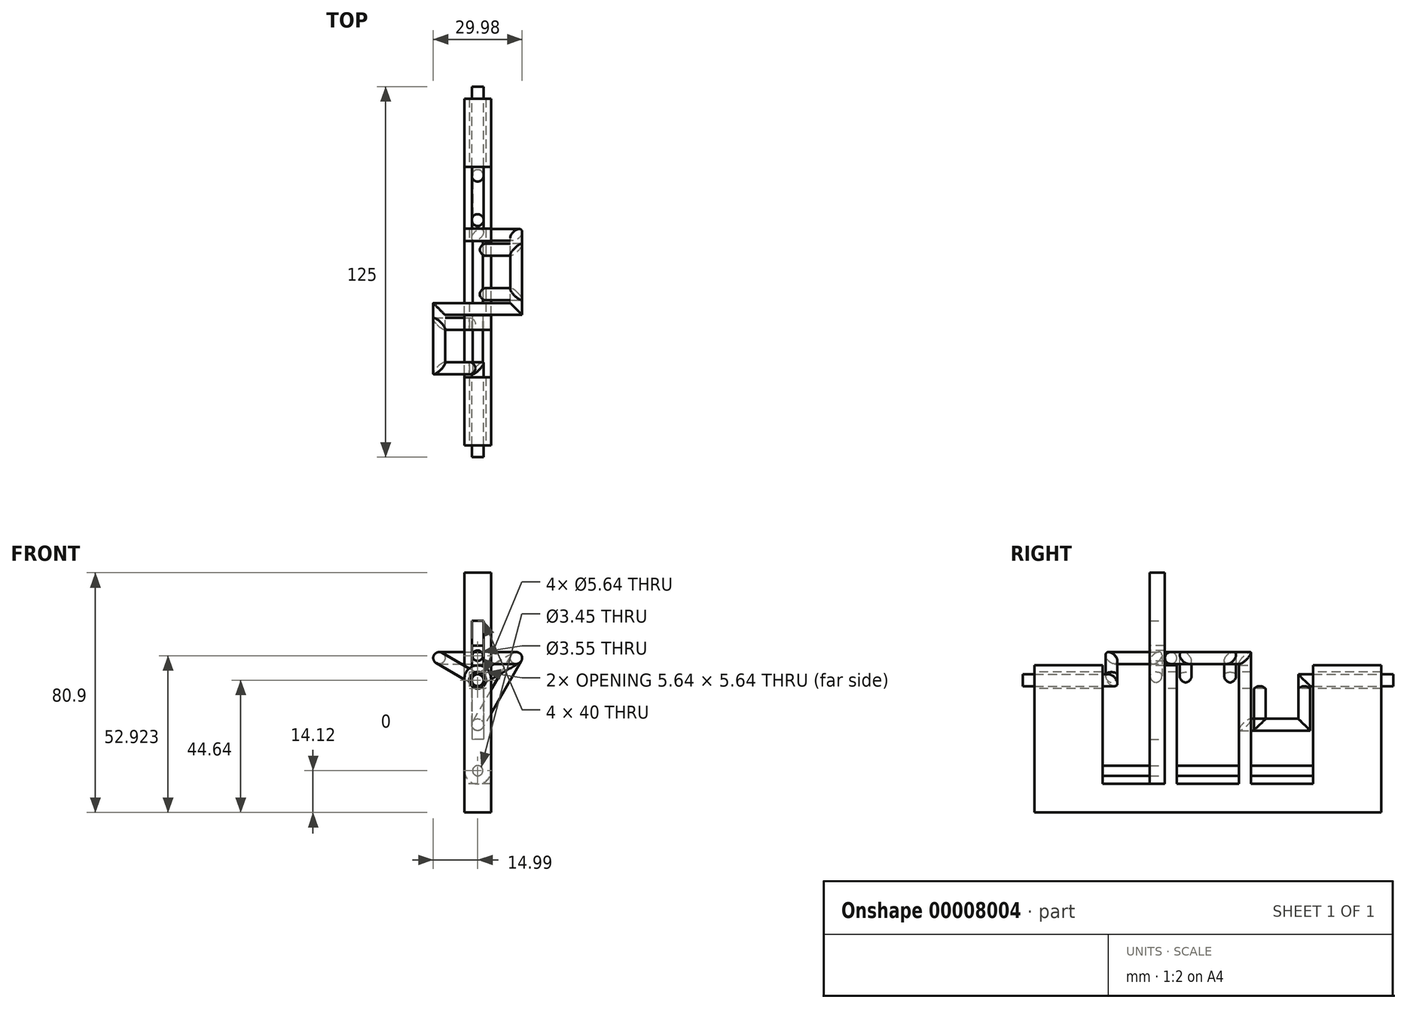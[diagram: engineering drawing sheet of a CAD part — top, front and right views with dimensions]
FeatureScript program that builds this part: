
annotation { "Feature Type Name" : "Feature", "Feature Type Description" : "" }
export const myFeature = defineFeature(function(context is Context, id is Id, definition is map)
    precondition{}
    {
        {
            var Q0;
            Q0=qCreatedBy(makeId("Front.planeOp"),FACE);
            var sketch = newSketch(context, id + "F0", { "sketchPlane" : qUnion([Q0])});
            skCircle(sketch, "E0", {"center": v(0, 0) * mm, "radius": 2 * mm});
            skLineSegment(sketch, "E1", {"start": v(0, 0) * mm, "end": v(-13, 7.5) * mm, "construction": true});
            skLineSegment(sketch, "E2", {"start": v(0, 0) * mm, "end": v(13, 7.5) * mm, "construction": true});
            skLineSegment(sketch, "E3", {"start": v(0, 0) * mm, "end": v(0, -15) * mm, "construction": true});
            skSolve(sketch);
        }
        {
            var Q0;
            Q0=qCreatedBy(makeId("Top.planeOp"),FACE);
            var sketch = newSketch(context, id + "F1", { "sketchPlane" : qUnion([Q0])});
            skLineSegment(sketch, "E4", {"start": v(0, 0) * mm, "end": v(0, 30) * mm});
            skLineSegment(sketch, "E5", {"start": v(0, 45) * mm, "end": v(0, 55) * mm});
            skLineSegment(sketch, "E6", {"start": v(0, 70) * mm, "end": v(0, 80) * mm});
            skLineSegment(sketch, "E7", {"start": v(0, 95) * mm, "end": v(0, 125) * mm});
            skLineSegment(sketch, "E8", {"start": v(0, 30) * mm, "end": v(0, 45) * mm, "construction": true});
            skLineSegment(sketch, "E9", {"start": v(0, 55) * mm, "end": v(0, 70) * mm, "construction": true});
            skLineSegment(sketch, "E10", {"start": v(0, 80) * mm, "end": v(0, 95) * mm, "construction": true});
            skSolve(sketch);
        }
        {
            var Q0;
            Q0=sQuery(id+"F0.wireOp",VERTEX,"E1.end");
            var Q1;
            Q1=sQuery(id+"F0.wireOp",VERTEX,"E2.start");
            var Q2;
            Q2=sQuery(id+"F1.wireOp",VERTEX,"E8.start");
            cPlane(context, id + "F2", {"entities" : qUnion([Q0, Q1, Q2]), "cplaneType" : CPlaneType.THREE_POINT, "offset" : 150 * mm, "width" : 150 * mm, "height" : 150 * mm});
        }
        {
            var Q0;
            Q0=sQuery(id+"F0.wireOp",VERTEX,"E2.end");
            var Q1;
            Q1=sQuery(id+"F0.wireOp",VERTEX,"E2.start");
            var Q2;
            Q2=sQuery(id+"F1.wireOp",VERTEX,"E8.start");
            cPlane(context, id + "F3", {"entities" : qUnion([Q0, Q1, Q2]), "cplaneType" : CPlaneType.THREE_POINT, "offset" : 150 * mm, "width" : 150 * mm, "height" : 150 * mm});
        }
        {
            var Q0;
            Q0=qCreatedBy(id+"F2.planeOp",FACE);
            var sketch = newSketch(context, id + "F4", { "sketchPlane" : qUnion([Q0])});
            skLineSegment(sketch, "E11.0", {"start": v(0, 0) * mm, "end": v(-15, 0) * mm, "construction": true});
            skLineSegment(sketch, "E12.0", {"start": v(0, -30) * mm, "end": v(0, -45) * mm, "construction": true});
            skLineSegment(sketch, "E13", {"start": v(0, -30) * mm, "end": v(-15, -30) * mm});
            skLineSegment(sketch, "E14", {"start": v(-15, -30) * mm, "end": v(-15, -45) * mm});
            skLineSegment(sketch, "E15", {"start": v(-15, -45) * mm, "end": v(0, -45) * mm});
            skSolve(sketch);
        }
        {
            var Q0;
            Q0=qCreatedBy(id+"F3.planeOp",FACE);
            var sketch = newSketch(context, id + "F5", { "sketchPlane" : qUnion([Q0])});
            skLineSegment(sketch, "E16.0", {"start": v(0, 0) * mm, "end": v(15, 0) * mm, "construction": true});
            skLineSegment(sketch, "E16.1", {"start": v(0, 55) * mm, "end": v(0, 70) * mm, "construction": true});
            skLineSegment(sketch, "E17", {"start": v(0, 55) * mm, "end": v(15, 55) * mm});
            skLineSegment(sketch, "E18", {"start": v(15, 55) * mm, "end": v(15, 70) * mm});
            skLineSegment(sketch, "E19", {"start": v(15, 70) * mm, "end": v(0, 70) * mm});
            skSolve(sketch);
        }
        {
            var Q0;
            Q0=qCreatedBy(makeId("Right.planeOp"),FACE);
            var sketch = newSketch(context, id + "F6", { "sketchPlane" : qUnion([Q0])});
            skLineSegment(sketch, "E20.0", {"start": v(0, 0) * mm, "end": v(0, -15) * mm, "construction": true});
            skLineSegment(sketch, "E20.1", {"start": v(80, 0) * mm, "end": v(95, 0) * mm, "construction": true});
            skLineSegment(sketch, "E21", {"start": v(80, 0) * mm, "end": v(80, -15) * mm});
            skLineSegment(sketch, "E22", {"start": v(80, -15) * mm, "end": v(95, -15) * mm});
            skLineSegment(sketch, "E23", {"start": v(95, -15) * mm, "end": v(95, 0) * mm});
            skSolve(sketch);
        }
        {
            var Q0;
            Q0=makeQuery(id+"F0.imprint","IMPRINT",FACE,{"disambiguationData":[TD([[makeQuery(id+"F0.imprint","IMPRINT",EDGE,{"derivedFrom":sQuery(id+"F0.wireOp",EDGE,"E0")}),1.0]])]});
            var Q1;
            Q1=sQuery(id+"F1.wireOp",EDGE,"E4");
            var Q2;
            Q2=sQuery(id+"F4.wireOp",EDGE,"E13");
            var Q3;
            Q3=sQuery(id+"F4.wireOp",EDGE,"E14");
            var Q4;
            Q4=sQuery(id+"F4.wireOp",EDGE,"E15");
            var Q5;
            Q5=sQuery(id+"F1.wireOp",EDGE,"E5");
            var Q6;
            Q6=sQuery(id+"F5.wireOp",EDGE,"E17");
            var Q7;
            Q7=sQuery(id+"F5.wireOp",EDGE,"E19");
            var Q8;
            Q8=sQuery(id+"F5.wireOp",EDGE,"E18");
            var Q9;
            Q9=sQuery(id+"F1.wireOp",EDGE,"E6");
            var Q10;
            Q10=sQuery(id+"F6.wireOp",EDGE,"E21");
            var Q11;
            Q11=sQuery(id+"F6.wireOp",EDGE,"E22");
            var Q12;
            Q12=sQuery(id+"F6.wireOp",EDGE,"E23");
            var Q13;
            Q13=sQuery(id+"F1.wireOp",EDGE,"E7");
            sweep(context, id + "F7", {"profiles" : qUnion([Q0]), "path" : qUnion([Q1, Q2, Q3, Q4, Q5, Q6, Q7, Q8, Q9, Q10, Q11, Q12, Q13])});
        }
        {
            var Q0;
            Q0=qCreatedBy(makeId("Right.planeOp"),FACE);
            var sketch = newSketch(context, id + "F8", { "sketchPlane" : qUnion([Q0])});
            skLineSegment(sketch, "E24", {"start": v(4, -44.64) * mm, "end": v(4, 5) * mm});
            skLineSegment(sketch, "E25", {"start": v(4, 5) * mm, "end": v(27, 5) * mm});
            skLineSegment(sketch, "E26", {"start": v(27, 5) * mm, "end": v(27, -35) * mm});
            skLineSegment(sketch, "E27", {"start": v(27, -35) * mm, "end": v(47.92, -35) * mm});
            skLineSegment(sketch, "E28", {"start": v(47.92, -35) * mm, "end": v(47.92, 5) * mm});
            skLineSegment(sketch, "E29", {"start": v(47.92, 5) * mm, "end": v(52.04, 5) * mm});
            skLineSegment(sketch, "E30", {"start": v(52.04, 5) * mm, "end": v(52.04, -35) * mm});
            skLineSegment(sketch, "E31", {"start": v(52.04, -35) * mm, "end": v(72.96, -35) * mm});
            skLineSegment(sketch, "E32", {"start": v(72.96, -35) * mm, "end": v(72.96, 5) * mm});
            skLineSegment(sketch, "E33", {"start": v(72.96, 5) * mm, "end": v(77.08, 5) * mm});
            skLineSegment(sketch, "E34", {"start": v(77.08, 5) * mm, "end": v(77.08, -35) * mm});
            skLineSegment(sketch, "E35", {"start": v(77.08, -35) * mm, "end": v(98, -35) * mm});
            skLineSegment(sketch, "E36", {"start": v(98, -35) * mm, "end": v(98, 5) * mm});
            skLineSegment(sketch, "E37", {"start": v(98, 5) * mm, "end": v(121, 5) * mm});
            skLineSegment(sketch, "E38", {"start": v(121, 5) * mm, "end": v(121, -44.64) * mm});
            skLineSegment(sketch, "E39", {"start": v(121, -44.64) * mm, "end": v(4, -44.64) * mm});
            skSolve(sketch);
        }
        {
            var Q0;
            Q0=makeQuery(id+"F8.imprint","IMPRINT",FACE,{"disambiguationData":[TD([[makeQuery(id+"F8.imprint","IMPRINT",EDGE,{"derivedFrom":sQuery(id+"F8.wireOp",EDGE,"E24")}),-1.0]])]});
            extrude(context, id + "F9", {"entities" : qUnion([Q0]), "endBound" : BoundingType.SYMMETRIC, "depth" : 9 * mm});
        }
        {
            var Q0;
            Q0=makeQuery(id+"F9.opExtrude","SWEPT_FACE",FACE,{"disambiguationData":[OSD([sQuery(id+"F8.wireOp",EDGE,"E24")])]});
            var sketch = newSketch(context, id + "F10", { "sketchPlane" : qUnion([Q0])});
            skCircle(sketch, "E40", {"center": v(0, 0) * mm, "radius": 2.82 * mm});
            skSolve(sketch);
        }
        {
            var Q0;
            Q0=makeQuery(id+"F9.opExtrude","CAP_FACE",FACE,{"disambiguationData":[OSD([sQuery(id+"F8.wireOp",EDGE,"E24"),sQuery(id+"F8.wireOp",EDGE,"E25"),sQuery(id+"F8.wireOp",EDGE,"E26"),sQuery(id+"F8.wireOp",EDGE,"E27"),sQuery(id+"F8.wireOp",EDGE,"E28"),sQuery(id+"F8.wireOp",EDGE,"E29"),sQuery(id+"F8.wireOp",EDGE,"E30"),sQuery(id+"F8.wireOp",EDGE,"E31"),sQuery(id+"F8.wireOp",EDGE,"E32"),sQuery(id+"F8.wireOp",EDGE,"E33"),sQuery(id+"F8.wireOp",EDGE,"E34"),sQuery(id+"F8.wireOp",EDGE,"E35"),sQuery(id+"F8.wireOp",EDGE,"E36"),sQuery(id+"F8.wireOp",EDGE,"E37"),sQuery(id+"F8.wireOp",EDGE,"E38"),sQuery(id+"F8.wireOp",EDGE,"E39")])],"isStart":false});
            var sketch = newSketch(context, id + "F11", { "sketchPlane" : qUnion([Q0])});
            skLineSegment(sketch, "E41.0.0", {"start": v(4, 5) * mm, "end": v(4, -44.64) * mm});
            skLineSegment(sketch, "E41.0.1", {"start": v(4, -44.64) * mm, "end": v(121, -44.64) * mm});
            skLineSegment(sketch, "E41.0.2", {"start": v(121, -44.64) * mm, "end": v(121, 5) * mm});
            skLineSegment(sketch, "E41.0.3", {"start": v(121, 5) * mm, "end": v(98, 5) * mm});
            skLineSegment(sketch, "E41.0.4", {"start": v(98, 5) * mm, "end": v(98, -35) * mm});
            skLineSegment(sketch, "E41.0.5", {"start": v(98, -35) * mm, "end": v(77.08, -35) * mm});
            skLineSegment(sketch, "E41.0.6", {"start": v(77.08, -35) * mm, "end": v(77.08, 5) * mm});
            skLineSegment(sketch, "E41.0.7", {"start": v(77.08, 5) * mm, "end": v(72.96, 5) * mm});
            skLineSegment(sketch, "E41.0.8", {"start": v(72.96, 5) * mm, "end": v(72.96, -35) * mm});
            skLineSegment(sketch, "E41.0.9", {"start": v(72.96, -35) * mm, "end": v(52.04, -35) * mm});
            skLineSegment(sketch, "E41.0.10", {"start": v(52.04, -35) * mm, "end": v(52.04, 5) * mm});
            skLineSegment(sketch, "E41.0.11", {"start": v(52.04, 5) * mm, "end": v(47.92, 5) * mm});
            skLineSegment(sketch, "E41.0.12", {"start": v(47.92, 5) * mm, "end": v(47.92, -35) * mm});
            skLineSegment(sketch, "E41.0.13", {"start": v(47.92, -35) * mm, "end": v(27, -35) * mm});
            skLineSegment(sketch, "E41.0.14", {"start": v(27, -35) * mm, "end": v(27, 5) * mm});
            skLineSegment(sketch, "E41.0.15", {"start": v(27, 5) * mm, "end": v(4, 5) * mm});
            skLineSegment(sketch, "E42", {"start": v(47.92, -35) * mm, "end": v(52.04, -35) * mm});
            skLineSegment(sketch, "E43", {"start": v(72.96, -35) * mm, "end": v(77.08, -35) * mm});
            skSolve(sketch);
        }
        {
            var Q0;
            Q0=makeQuery(id+"F11.imprint","IMPRINT",FACE,{"disambiguationData":[TD([[makeQuery(id+"F11.imprint","IMPRINT",EDGE,{"derivedFrom":sQuery(id+"F11.wireOp",EDGE,"E41.0.0")}),-1.0]])]});
            extrude(context, id + "F12", {"entities" : qUnion([Q0]), "oppositeDirection" : true, "depth" : 9 * mm});
        }
        {
            var Q0;
            Q0=makeQuery(id+"F10.imprint","IMPRINT",FACE,{"disambiguationData":[TD([[makeQuery(id+"F10.imprint","IMPRINT",EDGE,{"derivedFrom":sQuery(id+"F10.wireOp",EDGE,"E40")}),1.0]])]});
            extrude(context, id + "F13", {"entities" : qUnion([Q0]), "operationType" : NewBodyOperationType.REMOVE, "endBound" : BoundingType.THROUGH_ALL, "oppositeDirection" : true, "depth" : 25 * mm});
        }
        {
            var Q0;
            Q0=makeQuery(id+"F9.opExtrude","CAP_EDGE",EDGE,{"disambiguationData":[OSD([sQuery(id+"F8.wireOp",EDGE,"E25")])],"isStart":true});
            var Q1;
            Q1=makeQuery(id+"F9.opExtrude","CAP_EDGE",EDGE,{"disambiguationData":[OSD([sQuery(id+"F8.wireOp",EDGE,"E29")])],"isStart":false});
            var Q2;
            Q2=makeQuery(id+"F9.opExtrude","CAP_EDGE",EDGE,{"disambiguationData":[OSD([sQuery(id+"F8.wireOp",EDGE,"E29")])],"isStart":true});
            var Q3;
            Q3=makeQuery(id+"F9.opExtrude","CAP_EDGE",EDGE,{"disambiguationData":[OSD([sQuery(id+"F8.wireOp",EDGE,"E33")])],"isStart":false});
            var Q4;
            Q4=makeQuery(id+"F9.opExtrude","CAP_EDGE",EDGE,{"disambiguationData":[OSD([sQuery(id+"F8.wireOp",EDGE,"E33")])],"isStart":true});
            var Q5;
            Q5=makeQuery(id+"F9.opExtrude","CAP_EDGE",EDGE,{"disambiguationData":[OSD([sQuery(id+"F8.wireOp",EDGE,"E37")])],"isStart":false});
            var Q6;
            Q6=makeQuery(id+"F9.opExtrude","CAP_EDGE",EDGE,{"disambiguationData":[OSD([sQuery(id+"F8.wireOp",EDGE,"E37")])],"isStart":true});
            var Q7;
            Q7=makeQuery(id+"F9.opExtrude","CAP_EDGE",EDGE,{"disambiguationData":[OSD([sQuery(id+"F8.wireOp",EDGE,"E25")])],"isStart":false});
            var Q8;
            Q8=makeQuery(id+"F12.opExtrude","CAP_EDGE",EDGE,{"disambiguationData":[OSD([sQuery(id+"F11.wireOp",EDGE,"E41.0.15")])],"isStart":true});
            var Q9;
            Q9=makeQuery(id+"F12.opExtrude","CAP_EDGE",EDGE,{"disambiguationData":[OSD([sQuery(id+"F11.wireOp",EDGE,"E41.0.15")])],"isStart":false});
            var Q10;
            Q10=makeQuery(id+"F12.opExtrude","CAP_EDGE",EDGE,{"disambiguationData":[OSD([sQuery(id+"F11.wireOp",EDGE,"E41.0.3")])],"isStart":true});
            var Q11;
            Q11=makeQuery(id+"F12.opExtrude","CAP_EDGE",EDGE,{"disambiguationData":[OSD([sQuery(id+"F11.wireOp",EDGE,"E41.0.3")])],"isStart":false});
            fillet(context, id + "F14", {"entities" : qUnion([Q0, Q1, Q2, Q3, Q4, Q5, Q6, Q7, Q8, Q9, Q10, Q11]), "radius" : 4.5 * mm, "tangentPropagation" : true, "allowEdgeOverflow" : false});
        }
        {
            var Q0;
            Q0=qCreatedBy(id+"F2.planeOp",FACE);
            var sketch = newSketch(context, id + "F15", { "sketchPlane" : qUnion([Q0])});
            skLineSegment(sketch, "E44.0", {"start": v(0, -45) * mm, "end": v(0, -55) * mm, "construction": true});
            skLineSegment(sketch, "E44.1", {"start": v(0, 0) * mm, "end": v(-15, 0) * mm, "construction": true});
            skLineSegment(sketch, "E45.0", {"start": v(0, -30) * mm, "end": v(0, -45) * mm, "construction": true});
            skLineSegment(sketch, "E46", {"start": v(0, -30) * mm, "end": v(-15, -30) * mm});
            skLineSegment(sketch, "E47", {"start": v(0, -50) * mm, "end": v(-15, -50) * mm, "construction": true});
            skLineSegment(sketch, "E48", {"start": v(-15, -50) * mm, "end": v(-15, -30) * mm});
            skSolve(sketch);
        }
        {
            var Q0;
            Q0=qCreatedBy(id+"F3.planeOp",FACE);
            var sketch = newSketch(context, id + "F16", { "sketchPlane" : qUnion([Q0])});
            skLineSegment(sketch, "E49.0", {"start": v(0, 0) * mm, "end": v(15, 0) * mm, "construction": true});
            skPoint(sketch, "E49.1", {"position": v(0, 50) * mm});
            skLineSegment(sketch, "E49.2", {"start": v(0, 70) * mm, "end": v(0, 80) * mm, "construction": true});
            skLineSegment(sketch, "E50", {"start": v(0, 75) * mm, "end": v(15, 75) * mm, "construction": true});
            skLineSegment(sketch, "E51", {"start": v(15, 75) * mm, "end": v(15, 50) * mm});
            skSolve(sketch);
        }
        {
            var Q0;
            Q0=sQuery(id+"F16.wireOp",VERTEX,"E50.end");
            var Q1;
            Q1=sQuery(id+"F16.wireOp",VERTEX,"E51.end");
            var Q2;
            Q2=sQuery(id+"F15.wireOp",VERTEX,"E47.end");
            cPlane(context, id + "F17", {"entities" : qUnion([Q0, Q1, Q2]), "cplaneType" : CPlaneType.THREE_POINT, "offset" : 150 * mm, "width" : 150 * mm, "height" : 150 * mm});
        }
        {
            var Q0;
            Q0=qCreatedBy(id+"F17.planeOp",FACE);
            var sketch = newSketch(context, id + "F18", { "sketchPlane" : qUnion([Q0])});
            skPoint(sketch, "E52.0", {"position": v(13, 50) * mm});
            skPoint(sketch, "E52.1", {"position": v(-13, 50) * mm});
            skLineSegment(sketch, "E53", {"start": v(-13, 50) * mm, "end": v(13, 50) * mm});
            skSolve(sketch);
        }
        {
            var Q0;
            Q0=sQuery(id+"F6.wireOp",VERTEX,"E22.end");
            var Q1;
            Q1=sQuery(id+"F6.wireOp",VERTEX,"E22.start");
            var Q2;
            Q2=sQuery(id+"F16.wireOp",VERTEX,"E51.start");
            cPlane(context, id + "F19", {"entities" : qUnion([Q0, Q1, Q2]), "cplaneType" : CPlaneType.THREE_POINT, "offset" : 150 * mm, "width" : 150 * mm, "height" : 150 * mm});
        }
        {
            var Q0;
            Q0=qCreatedBy(id+"F19.planeOp",FACE);
            var sketch = newSketch(context, id + "F20", { "sketchPlane" : qUnion([Q0])});
            skPoint(sketch, "E54.0", {"position": v(95, -13) * mm});
            skPoint(sketch, "E54.1", {"position": v(75, 13) * mm});
            skLineSegment(sketch, "E55", {"start": v(75, 13) * mm, "end": v(75, -13) * mm});
            skLineSegment(sketch, "E56", {"start": v(75, -13) * mm, "end": v(95, -13) * mm});
            skSolve(sketch);
        }
        {
            var Q0;
            Q0=makeQuery(id+"F0.imprint","IMPRINT",FACE,{"disambiguationData":[TD([[makeQuery(id+"F0.imprint","IMPRINT",EDGE,{"derivedFrom":sQuery(id+"F0.wireOp",EDGE,"E0")}),1.0]])]});
            var Q1;
            Q1=sQuery(id+"F1.wireOp",EDGE,"E4");
            var Q2;
            Q2=sQuery(id+"F15.wireOp",EDGE,"E46");
            var Q3;
            Q3=sQuery(id+"F15.wireOp",EDGE,"E48");
            var Q4;
            Q4=sQuery(id+"F18.wireOp",EDGE,"E53");
            var Q5;
            Q5=sQuery(id+"F16.wireOp",EDGE,"E51");
            var Q6;
            Q6=sQuery(id+"F20.wireOp",EDGE,"E55");
            var Q7;
            Q7=sQuery(id+"F20.wireOp",EDGE,"E56");
            var Q8;
            Q8=sQuery(id+"F6.wireOp",EDGE,"E23");
            var Q9;
            Q9=sQuery(id+"F1.wireOp",EDGE,"E7");
            sweep(context, id + "F21", {"profiles" : qUnion([Q0]), "path" : qUnion([Q1, Q2, Q3, Q4, Q5, Q6, Q7, Q8, Q9])});
        }
        {
            var Q0;
            Q0=makeQuery(id+"F9.opExtrude","SWEPT_FACE",FACE,{"disambiguationData":[OSD([sQuery(id+"F8.wireOp",EDGE,"E26")])]});
            var sketch = newSketch(context, id + "F22", { "sketchPlane" : qUnion([Q0])});
            skCircle(sketch, "E57", {"center": v(0, -30.52) * mm, "radius": 1.73 * mm});
            skSolve(sketch);
        }
        {
            var Q0;
            Q0=makeQuery(id+"F22.imprint","IMPRINT",FACE,{"disambiguationData":[TD([[makeQuery(id+"F22.imprint","IMPRINT",EDGE,{"derivedFrom":sQuery(id+"F22.wireOp",EDGE,"E57")}),1.0]])]});
            extrude(context, id + "F23", {"entities" : qUnion([Q0]), "operationType" : NewBodyOperationType.ADD, "depth" : 75 * mm});
        }
        {
            var Q0;
            Q0=makeQuery(id+"F9.opExtrude","SWEPT_FACE",FACE,{"disambiguationData":[OSD([sQuery(id+"F8.wireOp",EDGE,"E28")])]});
            var sketch = newSketch(context, id + "F24", { "sketchPlane" : qUnion([Q0])});
            skCircle(sketch, "E58.0", {"center": v(0, -30.52) * mm, "radius": 1.73 * mm});
            skArc(sketch, "E59", {"start": v(-4.5, -30.52) * mm, "mid": v(0, -35.02) * mm, "end": v(4.5, -30.52) * mm});
            skLineSegment(sketch, "E60", {"start": v(-4.5, -30.52) * mm, "end": v(-4.5, 36.26) * mm});
            skLineSegment(sketch, "E61", {"start": v(-4.5, 36.26) * mm, "end": v(4.5, 36.26) * mm});
            skLineSegment(sketch, "E62", {"start": v(4.5, 36.26) * mm, "end": v(4.5, -30.52) * mm});
            skCircle(sketch, "E63.0", {"center": v(0, 0) * mm, "radius": 2 * mm, "construction": true});
            skLineSegment(sketch, "E64", {"start": v(-2, 20) * mm, "end": v(-2, -20) * mm});
            skLineSegment(sketch, "E65", {"start": v(2, 20) * mm, "end": v(2, -20) * mm});
            skLineSegment(sketch, "E66", {"start": v(2, -20) * mm, "end": v(-2, -20) * mm});
            skLineSegment(sketch, "E67", {"start": v(-2, 20) * mm, "end": v(2, 20) * mm});
            skSolve(sketch);
        }
        {
            var Q0;
            Q0 = qSketchRegion(id + "F24", true);
            extrude(context, id + "F25", {"entities" : qUnion([Q0]), "depth" : 5 * mm});
        }
        {
            var Q0;
            Q0=makeQuery(id+"F25.opExtrude","CAP_FACE",FACE,{"disambiguationData":[OSD([sQuery(id+"F24.wireOp",EDGE,"E58.0"),sQuery(id+"F24.wireOp",EDGE,"E59"),sQuery(id+"F24.wireOp",EDGE,"E60"),sQuery(id+"F24.wireOp",EDGE,"E61"),sQuery(id+"F24.wireOp",EDGE,"E62"),sQuery(id+"F24.wireOp",EDGE,"E64"),sQuery(id+"F24.wireOp",EDGE,"E65"),sQuery(id+"F24.wireOp",EDGE,"E66"),sQuery(id+"F24.wireOp",EDGE,"E67")])],"isStart":false});
            var sketch = newSketch(context, id + "F26", { "sketchPlane" : qUnion([Q0])});
            skLineSegment(sketch, "E68.bottom", {"start": v(-2, 4.95) * mm, "end": v(2, 4.95) * mm});
            skLineSegment(sketch, "E68.top", {"start": v(-2, 11.61) * mm, "end": v(2, 11.61) * mm});
            skLineSegment(sketch, "E68.left", {"start": v(-2, 4.95) * mm, "end": v(-2, 11.61) * mm});
            skLineSegment(sketch, "E68.right", {"start": v(2, 4.95) * mm, "end": v(2, 11.61) * mm});
            skLineSegment(sketch, "E69", {"start": v(-2, 8.28) * mm, "end": v(0, 8.28) * mm, "construction": true});
            skCircle(sketch, "E70", {"center": v(0, 8.28) * mm, "radius": 1.78 * mm});
            skSolve(sketch);
        }
        {
            var Q0;
            Q0=makeQuery(id+"F26.imprint","IMPRINT",FACE,{"disambiguationData":[TD([[makeQuery(id+"F26.imprint","IMPRINT",EDGE,{"derivedFrom":sQuery(id+"F26.wireOp",EDGE,"E68.bottom")}),1.0]])]});
            extrude(context, id + "F27", {"entities" : qUnion([Q0]), "oppositeDirection" : true, "depth" : 5 * mm});
        }
    });
